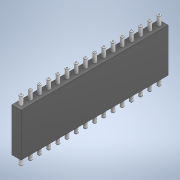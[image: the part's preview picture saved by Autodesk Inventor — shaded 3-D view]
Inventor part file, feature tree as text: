
AUTODESK INVENTOR PART (.ipt)
format: ipt  version: 2021 (Build 250183000, 183)  size: 166,912 bytes
history: native  units: in
note: dims shown in document units (in); Inventor stores cm internally (conversion verified against a paired STEP export)
features: extrude x2, sketch x2, fillet x1, pattern_linear x1, plane x1, mirror x1
ambient origin geometry x8: Origin, YZ Plane, XZ Plane, XY Plane, X Axis, Y Axis, Z Axis, Center Point
bodies: Solid1 (feature_tree)
feature tree (8):
  extrude  "Extrusion1"  Depth=0.1in
  extrude  "Extrusion2"  Depth=0.1in
  fillet  "Fillet1"  Radius=0.05in
  pattern_linear  "Rectangular Pattern1"  Spacing1=0.05in  [1 undecoded]
  plane  "Work Plane1"
  mirror  "Mirror1"
  sketch  "Sketch1"  dims[d0=1.6in d1=0.1in]
  sketch  "Sketch2"  dims[d2=0.4724in d3=0.0in d4=0.0354in d5=0.05in d6=0.05in d7=0.1in d8=0.0in d9=0.01in d10=6.2992in d12=0.1in]
note: 1 required parameter value undecoded (feature->parameter linkage not recoverable at this tier; creation-order binding heuristic only, values carry confidence <= 0.55)
